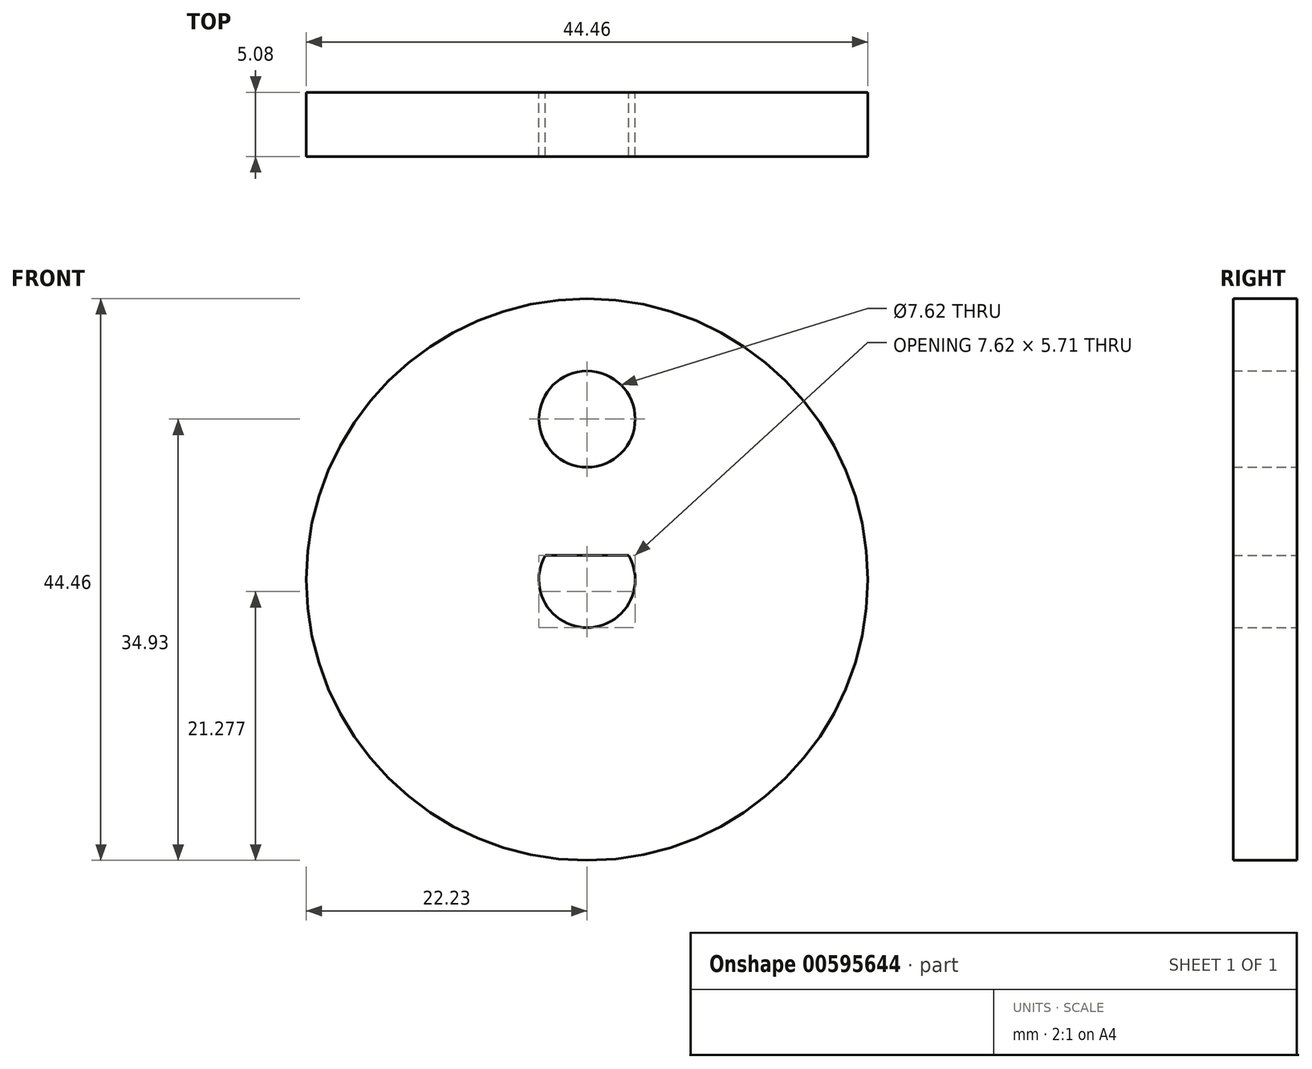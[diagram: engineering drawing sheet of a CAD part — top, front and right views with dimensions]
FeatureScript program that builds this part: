
annotation { "Feature Type Name" : "Feature", "Feature Type Description" : "" }
export const myFeature = defineFeature(function(context is Context, id is Id, definition is map)
    precondition{}
    {
        {
            var Q0;
            Q0=qCreatedBy(makeId("Front.planeOp"),FACE);
            var sketch = newSketch(context, id + "F0", { "sketchPlane" : qUnion([Q0])});
            skCircle(sketch, "E0", {"center": v(0, 0) * mm, "radius": 22.23 * mm});
            skCircle(sketch, "E1", {"center": v(0, 12.7) * mm, "radius": 3.81 * mm});
            skArc(sketch, "E2", {"start": v(-3.3, 1.9) * mm, "mid": v(0, -3.81) * mm, "end": v(3.3, 1.9) * mm});
            skLineSegment(sketch, "E3", {"start": v(-3.3, 1.9) * mm, "end": v(3.3, 1.9) * mm});
            skSolve(sketch);
        }
        {
            var Q0;
            Q0 = qSketchRegion(id + "F0", true);
            extrude(context, id + "F1", {"entities" : qUnion([Q0]), "depth" : 5.08 * mm, "offsetDistance" : 25.4 * mm});
        }
    });
